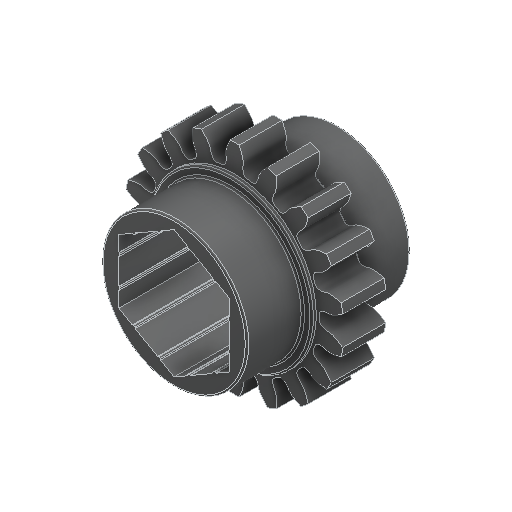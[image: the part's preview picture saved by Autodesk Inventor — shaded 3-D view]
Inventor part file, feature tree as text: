
AUTODESK INVENTOR PART (.ipt)
format: ipt  version: 2024.1 (Build 281209000, 209)  size: 396,800 bytes
history: native  units: in
note: dims shown in document units (in); Inventor stores cm internally (conversion verified against a paired STEP export)
features: fillet x1
ambient origin geometry x8: Origin, YZ Plane, XZ Plane, XY Plane, X Axis, Y Axis, Z Axis, Center Point
bodies: Solid1 (feature_tree)
feature tree (1):
  fillet  "Fillet1"  [1 undecoded]
note: 1 required parameter value undecoded (feature->parameter linkage not recoverable at this tier; creation-order binding heuristic only, values carry confidence <= 0.55)
